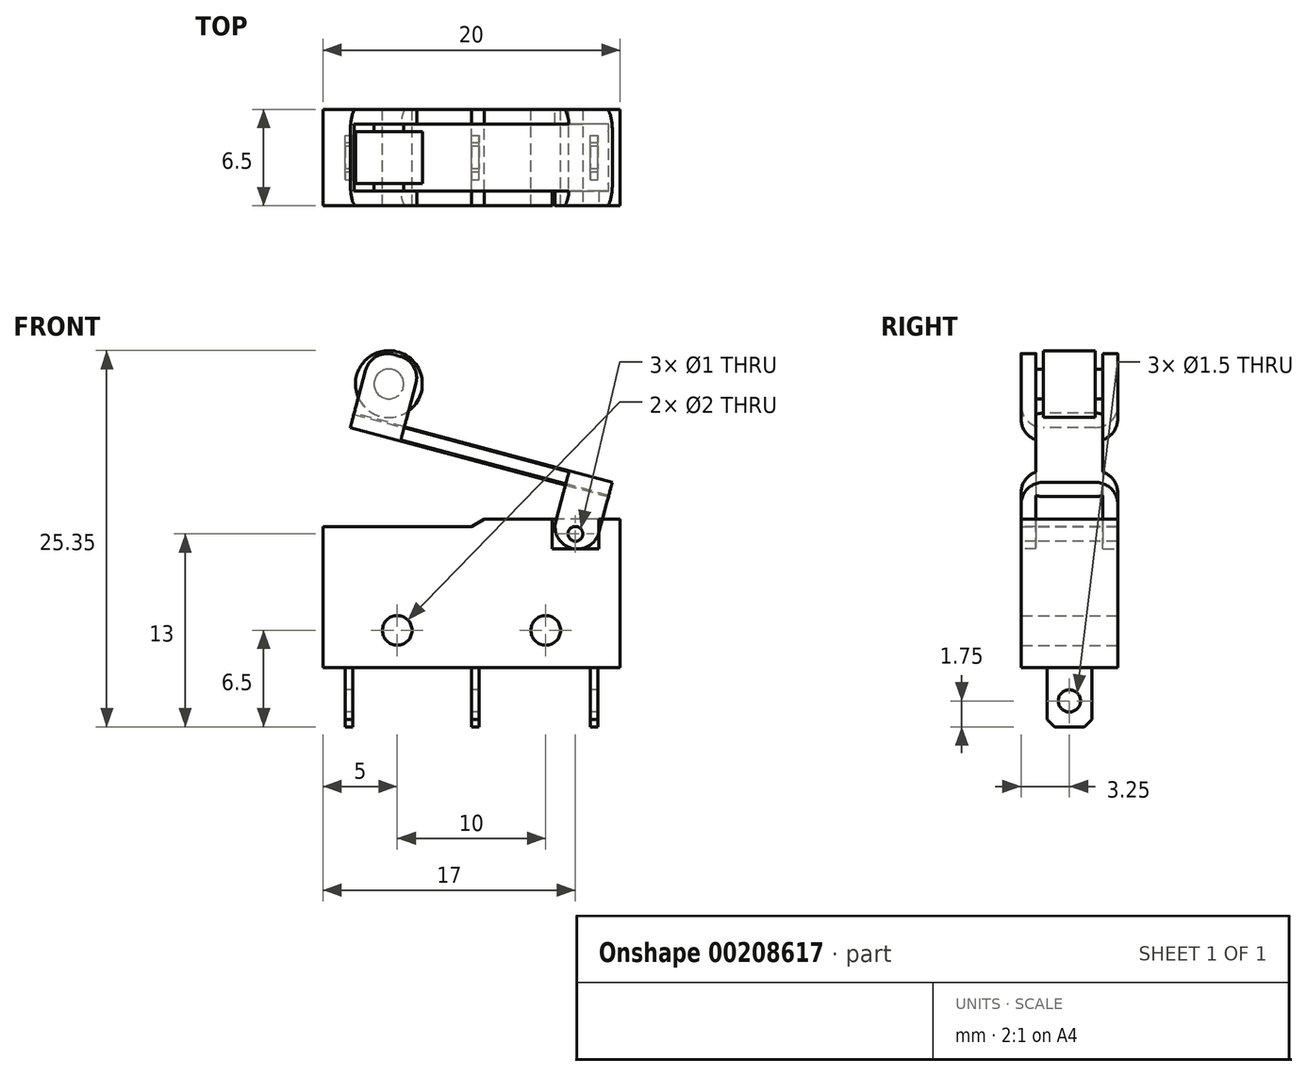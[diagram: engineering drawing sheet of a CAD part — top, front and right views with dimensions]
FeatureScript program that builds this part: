
annotation { "Feature Type Name" : "Feature", "Feature Type Description" : "" }
export const myFeature = defineFeature(function(context is Context, id is Id, definition is map)
    precondition{}
    {
        {
            var Q0;
            Q0=qCreatedBy(makeId("Front.planeOp"),FACE);
            var sketch = newSketch(context, id + "F0", { "sketchPlane" : qUnion([Q0])});
            skLineSegment(sketch, "E0.bottom", {"start": v(10, -5) * mm, "end": v(-10, -5) * mm});
            skLineSegment(sketch, "E0.top", {"start": v(10, 5) * mm, "end": v(0.87, 5) * mm});
            skLineSegment(sketch, "E0.left", {"start": v(10, -5) * mm, "end": v(10, 5) * mm});
            skLineSegment(sketch, "E0.right", {"start": v(-10, -5) * mm, "end": v(-10, 4.5) * mm});
            skPoint(sketch, "E0.middle", {"position": v(0, 0) * mm});
            skLineSegment(sketch, "E1", {"start": v(0.87, 5) * mm, "end": v(-10, 5) * mm, "construction": true});
            skLineSegment(sketch, "E2", {"start": v(0.87, 5) * mm, "end": v(0, 4.5) * mm});
            skLineSegment(sketch, "E3", {"start": v(-10, 4.5) * mm, "end": v(-10, 5) * mm, "construction": true});
            skLineSegment(sketch, "E4", {"start": v(0, 4.5) * mm, "end": v(-10, 4.5) * mm});
            skCircle(sketch, "E5", {"center": v(-5, -2.5) * mm, "radius": 1 * mm});
            skCircle(sketch, "E6", {"center": v(5, -2.5) * mm, "radius": 1 * mm});
            skLineSegment(sketch, "E7", {"start": v(-5, -2.5) * mm, "end": v(5, -2.5) * mm, "construction": true});
            skLineSegment(sketch, "E8", {"start": v(0, -2.5) * mm, "end": v(0, 0) * mm, "construction": true});
            skPoint(sketch, "E9", {"position": v(7, 4) * mm});
            skLineSegment(sketch, "E10", {"start": v(7, 4) * mm, "end": v(7.4, 5.48) * mm, "construction": true});
            skSolve(sketch);
        }
        {
            var Q0;
            Q0 = qSketchRegion(id + "F0", true);
            extrude(context, id + "F1", {"entities" : qUnion([Q0]), "endBound" : BoundingType.SYMMETRIC, "depth" : 6.5 * mm});
        }
        {
            var Q0;
            Q0=qCreatedBy(makeId("Front.planeOp"),FACE);
            var sketch = newSketch(context, id + "F2", { "sketchPlane" : qUnion([Q0])});
            skLineSegment(sketch, "E11.bottom", {"start": v(-8.5, -5) * mm, "end": v(-8, -5) * mm});
            skLineSegment(sketch, "E11.top", {"start": v(-8.5, -9) * mm, "end": v(-8, -9) * mm});
            skLineSegment(sketch, "E11.left", {"start": v(-8.5, -5) * mm, "end": v(-8.5, -9) * mm});
            skLineSegment(sketch, "E11.right", {"start": v(-8, -5) * mm, "end": v(-8, -9) * mm});
            skLineSegment(sketch, "E12.bottom", {"start": v(0, -5) * mm, "end": v(0.5, -5) * mm});
            skLineSegment(sketch, "E12.top", {"start": v(0, -9) * mm, "end": v(0.5, -9) * mm});
            skLineSegment(sketch, "E12.left", {"start": v(0, -5) * mm, "end": v(0, -9) * mm});
            skLineSegment(sketch, "E12.right", {"start": v(0.5, -5) * mm, "end": v(0.5, -9) * mm});
            skLineSegment(sketch, "E13.bottom", {"start": v(8, -5) * mm, "end": v(8.5, -5) * mm});
            skLineSegment(sketch, "E13.top", {"start": v(8, -9) * mm, "end": v(8.5, -9) * mm});
            skLineSegment(sketch, "E13.left", {"start": v(8, -5) * mm, "end": v(8, -9) * mm});
            skLineSegment(sketch, "E13.right", {"start": v(8.5, -5) * mm, "end": v(8.5, -9) * mm});
            skSolve(sketch);
        }
        {
            var Q0;
            Q0 = qSketchRegion(id + "F2", true);
            extrude(context, id + "F3", {"entities" : qUnion([Q0]), "operationType" : NewBodyOperationType.ADD, "endBound" : BoundingType.SYMMETRIC, "depth" : 3 * mm});
        }
        {
            var Q0;
            Q0=makeQuery(id+"F3.opExtrude","SWEPT_FACE",FACE,{"disambiguationData":[OSD([sQuery(id+"F2.wireOp",EDGE,"E11.left")])]});
            var sketch = newSketch(context, id + "F4", { "sketchPlane" : qUnion([Q0])});
            skLineSegment(sketch, "E14", {"start": v(0, -9) * mm, "end": v(0, -7.25) * mm, "construction": true});
            skPoint(sketch, "E14.endSnap0", {"position": v(0, -9) * mm});
            skCircle(sketch, "E15", {"center": v(0, -7.25) * mm, "radius": 0.75 * mm});
            skSolve(sketch);
        }
        {
            var Q0;
            Q0 = qSketchRegion(id + "F4", true);
            extrude(context, id + "F5", {"entities" : qUnion([Q0]), "operationType" : NewBodyOperationType.REMOVE, "endBound" : BoundingType.THROUGH_ALL, "oppositeDirection" : true, "depth" : 25 * mm});
        }
        {
            var Q0;
            Q0=makeQuery(id+"F3.opExtrude","CAP_EDGE",EDGE,{"disambiguationData":[OSD([sQuery(id+"F2.wireOp",EDGE,"E11.top")])],"isStart":false});
            var Q1;
            Q1=makeQuery(id+"F3.opExtrude","CAP_EDGE",EDGE,{"disambiguationData":[OSD([sQuery(id+"F2.wireOp",EDGE,"E12.top")])],"isStart":false});
            var Q2;
            Q2=makeQuery(id+"F3.opExtrude","CAP_EDGE",EDGE,{"disambiguationData":[OSD([sQuery(id+"F2.wireOp",EDGE,"E13.top")])],"isStart":false});
            var Q3;
            Q3=makeQuery(id+"F3.opExtrude","CAP_EDGE",EDGE,{"disambiguationData":[OSD([sQuery(id+"F2.wireOp",EDGE,"E11.top")])],"isStart":true});
            var Q4;
            Q4=makeQuery(id+"F3.opExtrude","CAP_EDGE",EDGE,{"disambiguationData":[OSD([sQuery(id+"F2.wireOp",EDGE,"E12.top")])],"isStart":true});
            var Q5;
            Q5=makeQuery(id+"F3.opExtrude","CAP_EDGE",EDGE,{"disambiguationData":[OSD([sQuery(id+"F2.wireOp",EDGE,"E13.top")])],"isStart":true});
            chamfer(context, id + "F6", {"entities" : qUnion([Q0, Q1, Q2, Q3, Q4, Q5]), "width" : .5 * mm, "tangentPropagation" : true});
        }
        {
            var Q0;
            Q0=makeQuery(id+"F1.opExtrude","CAP_FACE",FACE,{"disambiguationData":[OSD([sQuery(id+"F0.wireOp",EDGE,"E0.bottom"),sQuery(id+"F0.wireOp",EDGE,"E0.top"),sQuery(id+"F0.wireOp",EDGE,"E0.left"),sQuery(id+"F0.wireOp",EDGE,"E0.right"),sQuery(id+"F0.wireOp",EDGE,"E2"),sQuery(id+"F0.wireOp",EDGE,"E4"),sQuery(id+"F0.wireOp",EDGE,"E5"),sQuery(id+"F0.wireOp",EDGE,"E6")])],"isStart":false});
            var sketch = newSketch(context, id + "F7", { "sketchPlane" : qUnion([Q0])});
            skCircle(sketch, "E16", {"center": v(7, 4) * mm, "radius": 0.5 * mm});
            skLineSegment(sketch, "E17.bottom", {"start": v(5.43, 5) * mm, "end": v(8.57, 5) * mm});
            skLineSegment(sketch, "E17.top", {"start": v(5.43, 3) * mm, "end": v(8.57, 3) * mm});
            skLineSegment(sketch, "E17.left", {"start": v(5.43, 5) * mm, "end": v(5.43, 3) * mm});
            skLineSegment(sketch, "E17.right", {"start": v(8.57, 5) * mm, "end": v(8.57, 3) * mm});
            skLineSegment(sketch, "E18", {"start": v(7, 5) * mm, "end": v(7, 4) * mm, "construction": true});
            skLineSegment(sketch, "E19", {"start": v(7, 4) * mm, "end": v(7, 3) * mm, "construction": true});
            skSolve(sketch);
        }
        {
            var Q0;
            Q0 = qSketchRegion(id + "F7", true);
            extrude(context, id + "F8", {"entities" : qUnion([Q0]), "operationType" : NewBodyOperationType.REMOVE, "oppositeDirection" : true, "depth" : 1 * mm});
        }
        {
            var Q0;
            Q0=sQuery(id+"F0.wireOp",VERTEX,"E9");
            var Q1;
            Q1=sQuery(id+"F0.wireOp",EDGE,"E10");
            cPlane(context, id + "F9", {"entities" : qUnion([Q0, Q1]), "cplaneType" : CPlaneType.LINE_POINT, "offset" : 25 * mm, "width" : 150 * mm, "height" : 150 * mm});
        }
        {
            var Q0;
            Q0=qCreatedBy(id+"F9.planeOp",FACE);
            var sketch = newSketch(context, id + "F10", { "sketchPlane" : qUnion([Q0])});
            skLineSegment(sketch, "E20.bottom", {"start": v(4.23, 3.25) * mm, "end": v(7.23, 3.25) * mm});
            skLineSegment(sketch, "E20.top", {"start": v(4.23, 2.25) * mm, "end": v(7.23, 2.25) * mm});
            skLineSegment(sketch, "E20.left", {"start": v(4.23, 3.25) * mm, "end": v(4.23, 2.25) * mm});
            skLineSegment(sketch, "E20.right", {"start": v(7.23, 3.25) * mm, "end": v(7.23, 2.25) * mm});
            skLineSegment(sketch, "E21", {"start": v(5.73, 2.25) * mm, "end": v(5.73, 3.25) * mm, "construction": true});
            skLineSegment(sketch, "E22.MirrorCS", {"start": v(4.23, -2.25) * mm, "end": v(7.23, -2.25) * mm});
            skLineSegment(sketch, "E23.MirrorCS", {"start": v(4.23, -3.25) * mm, "end": v(7.23, -3.25) * mm});
            skLineSegment(sketch, "E24.MirrorCS", {"start": v(4.23, -3.25) * mm, "end": v(4.23, -2.25) * mm});
            skLineSegment(sketch, "E25.MirrorCS", {"start": v(7.23, -3.25) * mm, "end": v(7.23, -2.25) * mm});
            skLineSegment(sketch, "E26.MirrorCS", {"start": v(5.73, -2.25) * mm, "end": v(5.73, -3.25) * mm, "construction": true});
            skSolve(sketch);
        }
        {
            var Q0;
            Q0 = qSketchRegion(id + "F10", true);
            extrude(context, id + "F11", {"entities" : qUnion([Q0]), "depth" : 3 * mm, "hasSecondDirection" : true, "secondDirectionOppositeDirection" : true, "secondDirectionDepth" : 1 * mm});
        }
        {
            var Q0;
            Q0=qCreatedBy(makeId("Front.planeOp"),FACE);
            var sketch = newSketch(context, id + "F12", { "sketchPlane" : qUnion([Q0])});
            skCircle(sketch, "E27", {"center": v(7, 4) * mm, "radius": 0.5 * mm});
            skSolve(sketch);
        }
        {
            var Q0;
            Q0 = qSketchRegion(id + "F12", true);
            extrude(context, id + "F13", {"entities" : qUnion([Q0]), "operationType" : NewBodyOperationType.REMOVE, "endBound" : BoundingType.SYMMETRIC, "oppositeDirection" : true, "depth" : 25 * mm});
        }
        {
            var Q0;
            Q0=makeQuery(id+"F11.opExtrude","CAP_FACE",FACE,{"disambiguationData":[OSD([sQuery(id+"F10.wireOp",EDGE,"E20.bottom"),sQuery(id+"F10.wireOp",EDGE,"E20.top"),sQuery(id+"F10.wireOp",EDGE,"E20.left"),sQuery(id+"F10.wireOp",EDGE,"E20.right")])],"isStart":false});
            var sketch = newSketch(context, id + "F14", { "sketchPlane" : qUnion([Q0])});
            skLineSegment(sketch, "E28.bottom", {"start": v(7.23, 3.25) * mm, "end": v(4.23, 3.25) * mm});
            skLineSegment(sketch, "E28.top", {"start": v(7.23, -3.25) * mm, "end": v(4.23, -3.25) * mm});
            skLineSegment(sketch, "E28.left", {"start": v(7.23, 3.25) * mm, "end": v(7.23, -3.25) * mm});
            skLineSegment(sketch, "E28.right", {"start": v(-10.77, 3.25) * mm, "end": v(-10.77, 2.25) * mm, "construction": true});
            skLineSegment(sketch, "E29", {"start": v(4.23, 3.25) * mm, "end": v(-10.77, 3.25) * mm, "construction": true});
            skLineSegment(sketch, "E30", {"start": v(4.23, 3.25) * mm, "end": v(4.23, 2.25) * mm});
            skLineSegment(sketch, "E31", {"start": v(4.23, 2.25) * mm, "end": v(-10.77, 2.25) * mm});
            skLineSegment(sketch, "E32", {"start": v(-10.77, 2.25) * mm, "end": v(-10.77, -2.25) * mm});
            skLineSegment(sketch, "E33", {"start": v(-10.77, -2.25) * mm, "end": v(4.23, -2.25) * mm});
            skLineSegment(sketch, "E34", {"start": v(4.23, -2.25) * mm, "end": v(4.23, -3.25) * mm});
            skSolve(sketch);
        }
        {
            var Q0;
            Q0 = qSketchRegion(id + "F14", true);
            extrude(context, id + "F15", {"entities" : qUnion([Q0]), "operationType" : NewBodyOperationType.ADD, "depth" : 1 * mm});
        }
        {
            var Q0;
            Q0=makeQuery(id+"F15.opExtrude","CAP_FACE",FACE,{"disambiguationData":[OSD([sQuery(id+"F14.wireOp",EDGE,"E28.bottom"),sQuery(id+"F14.wireOp",EDGE,"E28.top"),sQuery(id+"F14.wireOp",EDGE,"E28.left"),sQuery(id+"F14.wireOp",EDGE,"E30"),sQuery(id+"F14.wireOp",EDGE,"E31"),sQuery(id+"F14.wireOp",EDGE,"E32"),sQuery(id+"F14.wireOp",EDGE,"E33"),sQuery(id+"F14.wireOp",EDGE,"E34")])],"isStart":true});
            var sketch = newSketch(context, id + "F16", { "sketchPlane" : qUnion([Q0])});
            skLineSegment(sketch, "E35.bottom", {"start": v(-10.77, -2.25) * mm, "end": v(-7.27, -2.25) * mm});
            skLineSegment(sketch, "E35.top", {"start": v(-10.77, -3.25) * mm, "end": v(-7.27, -3.25) * mm});
            skLineSegment(sketch, "E35.left", {"start": v(-10.77, -2.25) * mm, "end": v(-10.77, -3.25) * mm});
            skLineSegment(sketch, "E35.right", {"start": v(-7.27, -2.25) * mm, "end": v(-7.27, -3.25) * mm});
            skLineSegment(sketch, "E36.MirrorCS", {"start": v(-7.27, 2.25) * mm, "end": v(-7.27, 3.25) * mm});
            skLineSegment(sketch, "E37.MirrorCS", {"start": v(-10.77, 2.25) * mm, "end": v(-10.77, 3.25) * mm});
            skLineSegment(sketch, "E38.MirrorCS", {"start": v(-10.77, 3.25) * mm, "end": v(-7.27, 3.25) * mm});
            skLineSegment(sketch, "E39.MirrorCS", {"start": v(-10.77, 2.25) * mm, "end": v(-7.27, 2.25) * mm});
            skSolve(sketch);
        }
        {
            var Q0;
            Q0 = qSketchRegion(id + "F16", true);
            extrude(context, id + "F17", {"entities" : qUnion([Q0]), "operationType" : NewBodyOperationType.ADD, "oppositeDirection" : true, "depth" : 5.5 * mm});
        }
        {
            var Q0;
            Q0=makeQuery(id+"F15.opExtrude","CAP_FACE",FACE,{"disambiguationData":[OSD([sQuery(id+"F14.wireOp",EDGE,"E28.bottom"),sQuery(id+"F14.wireOp",EDGE,"E28.top"),sQuery(id+"F14.wireOp",EDGE,"E28.left"),sQuery(id+"F14.wireOp",EDGE,"E30"),sQuery(id+"F14.wireOp",EDGE,"E31"),sQuery(id+"F14.wireOp",EDGE,"E32"),sQuery(id+"F14.wireOp",EDGE,"E33"),sQuery(id+"F14.wireOp",EDGE,"E34")])],"isStart":false});
            cPlane(context, id + "F18", {"entities" : qUnion([Q0]), "cplaneType" : CPlaneType.OFFSET, "offset" : 2.5 * mm, "width" : 150 * mm, "height" : 150 * mm});
        }
        {
            var Q0;
            Q0=qCreatedBy(id+"F18.planeOp",FACE);
            var sketch = newSketch(context, id + "F19", { "sketchPlane" : qUnion([Q0])});
            skLineSegment(sketch, "E40", {"start": v(-9.02, 2.25) * mm, "end": v(-9.02, 0) * mm});
            skLineSegment(sketch, "E41", {"start": v(-8.02, 2.25) * mm, "end": v(-8.02, 1.75) * mm});
            skLineSegment(sketch, "E42", {"start": v(-8.02, 1.75) * mm, "end": v(-6.77, 1.75) * mm});
            skLineSegment(sketch, "E43", {"start": v(-6.77, 1.75) * mm, "end": v(-6.77, 0) * mm});
            skLineSegment(sketch, "E44", {"start": v(-8.02, 2.25) * mm, "end": v(-9.02, 2.25) * mm});
            skLineSegment(sketch, "E45", {"start": v(-9.02, 0) * mm, "end": v(-6.77, 0) * mm, "construction": true});
            skLineSegment(sketch, "E46.MirrorCS", {"start": v(-9.02, -2.25) * mm, "end": v(-9.02, 0) * mm});
            skLineSegment(sketch, "E47.MirrorCS", {"start": v(-8.02, -2.25) * mm, "end": v(-8.02, -1.75) * mm});
            skLineSegment(sketch, "E48.MirrorCS", {"start": v(-8.02, -1.75) * mm, "end": v(-6.77, -1.75) * mm});
            skLineSegment(sketch, "E49.MirrorCS", {"start": v(-6.77, -1.75) * mm, "end": v(-6.77, 0) * mm});
            skLineSegment(sketch, "E50.MirrorCS", {"start": v(-8.02, -2.25) * mm, "end": v(-9.02, -2.25) * mm});
            skSolve(sketch);
        }
        {
            var Q0;
            Q0 = qSketchRegion(id + "F19", true);
            var Q1;
            Q1=sQuery(id+"F19.wireOp",EDGE,"E40");
            revolve(context, id + "F20", {"operationType" : NewBodyOperationType.ADD, "entities" : qUnion([Q0]), "axis" : qUnion([Q1]), "revolveType" : RevolveType.FULL});
        }
        {
            var Q0;
            Q0=makeQuery(id+"F17.opExtrude","CAP_EDGE",EDGE,{"disambiguationData":[OSD([sQuery(id+"F16.wireOp",EDGE,"E37.MirrorCS")])],"isStart":false});
            var Q1;
            Q1=makeQuery(id+"F17.opExtrude","CAP_EDGE",EDGE,{"disambiguationData":[OSD([sQuery(id+"F16.wireOp",EDGE,"E36.MirrorCS")])],"isStart":false});
            var Q2;
            Q2=makeQuery(id+"F17.opExtrude","CAP_EDGE",EDGE,{"disambiguationData":[OSD([sQuery(id+"F16.wireOp",EDGE,"E35.right")])],"isStart":false});
            var Q3;
            Q3=makeQuery(id+"F17.opExtrude","CAP_EDGE",EDGE,{"disambiguationData":[OSD([sQuery(id+"F16.wireOp",EDGE,"E35.left")])],"isStart":false});
            var Q4;
            Q4=makeQuery(id+"F11.opExtrude","CAP_EDGE",EDGE,{"disambiguationData":[OSD([sQuery(id+"F10.wireOp",EDGE,"E24.MirrorCS")])],"isStart":true});
            var Q5;
            Q5=makeQuery(id+"F11.opExtrude","CAP_EDGE",EDGE,{"disambiguationData":[OSD([sQuery(id+"F10.wireOp",EDGE,"E25.MirrorCS")])],"isStart":true});
            var Q6;
            Q6=makeQuery(id+"F11.opExtrude","CAP_EDGE",EDGE,{"disambiguationData":[OSD([sQuery(id+"F10.wireOp",EDGE,"E20.right")])],"isStart":true});
            var Q7;
            Q7=makeQuery(id+"F11.opExtrude","CAP_EDGE",EDGE,{"disambiguationData":[OSD([sQuery(id+"F10.wireOp",EDGE,"E20.left")])],"isStart":true});
            var Q8;
            Q8=makeQuery(id+"F15.opExtrude","CAP_EDGE",EDGE,{"disambiguationData":[OSD([sQuery(id+"F14.wireOp",EDGE,"E28.top")])],"isStart":false});
            var Q9;
            Q9=makeQuery(id+"F15.opExtrude","CAP_EDGE",EDGE,{"disambiguationData":[OSD([sQuery(id+"F14.wireOp",EDGE,"E28.bottom")])],"isStart":false});
            var Q10;
            Q10=makeQuery(id+"F17.opExtrude","CAP_EDGE",EDGE,{"disambiguationData":[OSD([sQuery(id+"F16.wireOp",EDGE,"E38.MirrorCS")])],"isStart":true});
            var Q11;
            Q11=makeQuery(id+"F17.opExtrude","CAP_EDGE",EDGE,{"disambiguationData":[OSD([sQuery(id+"F16.wireOp",EDGE,"E35.top")])],"isStart":true});
            fillet(context, id + "F21", {"entities" : qUnion([Q0, Q1, Q2, Q3, Q4, Q5, Q6, Q7, Q8, Q9, Q10, Q11]), "radius" : 1.5 * mm, "tangentPropagation" : true, "allowEdgeOverflow" : false});
        }
    });
